# Revit family: Gira_012828
name_source: partatom
category: Electrical Fixtures
revit_build: Autodesk Revit 2017 (Build: 20160225_1515(x64)
units: mm (PartAtom-declared; Revit-internal decimal feet)

## family parameters
Cut with Voids When Loaded = No
Host = Face
Maintain Annotation Orientation = Yes
Part Type = Normal
Room Calculation Point = No
Round Connector Dimension = Use Diameter
Shared = No

## types (1)
- PB sw. 2-way 2-g System 55 anthra.
    Assembly arrangement = Basic element with central cover plate
    Available = No
    BIM (1) = https://media.stage.bim.site und Tasten.rfa?public/gira/36a6b08/Sys55_Komplettgerät_Schalten und Tasten.rfa
    Category = Switch
    Colour = Anthracite
    Connection type = Plug clamp
    Data sheet (1) = https://katalog.gira.de
    Default Elevation = 1219 mm
    Description = PB sw.2-w 2g Sys55 AN,Pushbutton switch, 10 AX 250 V~ with rocker, 2-gang,2-way switch, 2-gang,anthracite,
    GTIN = 4010337128281
    HAN = 012828
    Halogen free = Yes
    HeinzeBIM = https://bimportal.heinze.de
    Illumination = No
    Label space/information surface = No
    Manufacturer = Gira
    Manufacturer URL = https://www.gira.de
    Material = Plastic
    Material quality = Thermoplastic
    Method of operation = Rocker/button
    Model = Sys55_Komplettgerät_Schalten und Tasten
    Mounting method = Flush mounted (plaster)
    Name = PB sw. 2-way 2-g System 55 anthra.
    Nominal voltage = 250
    Number of modules (module system) = 1
    Number of rockers = 2
    Push button switch = Yes
    Rated current = 10
    Suitable for degree of protection (IP) = IP20
    Surface protection = Other
    Type of fastening = Mounting with claw and screw
    URL = http://katalog.gira.de
    Washing machine switch = No
    Wiring system = Alternating-/alternating switch
    With mounting plate = No

## geometry (parser evidence)
native form markers: Sweep x7
no freeform markers — native parametric forms only
